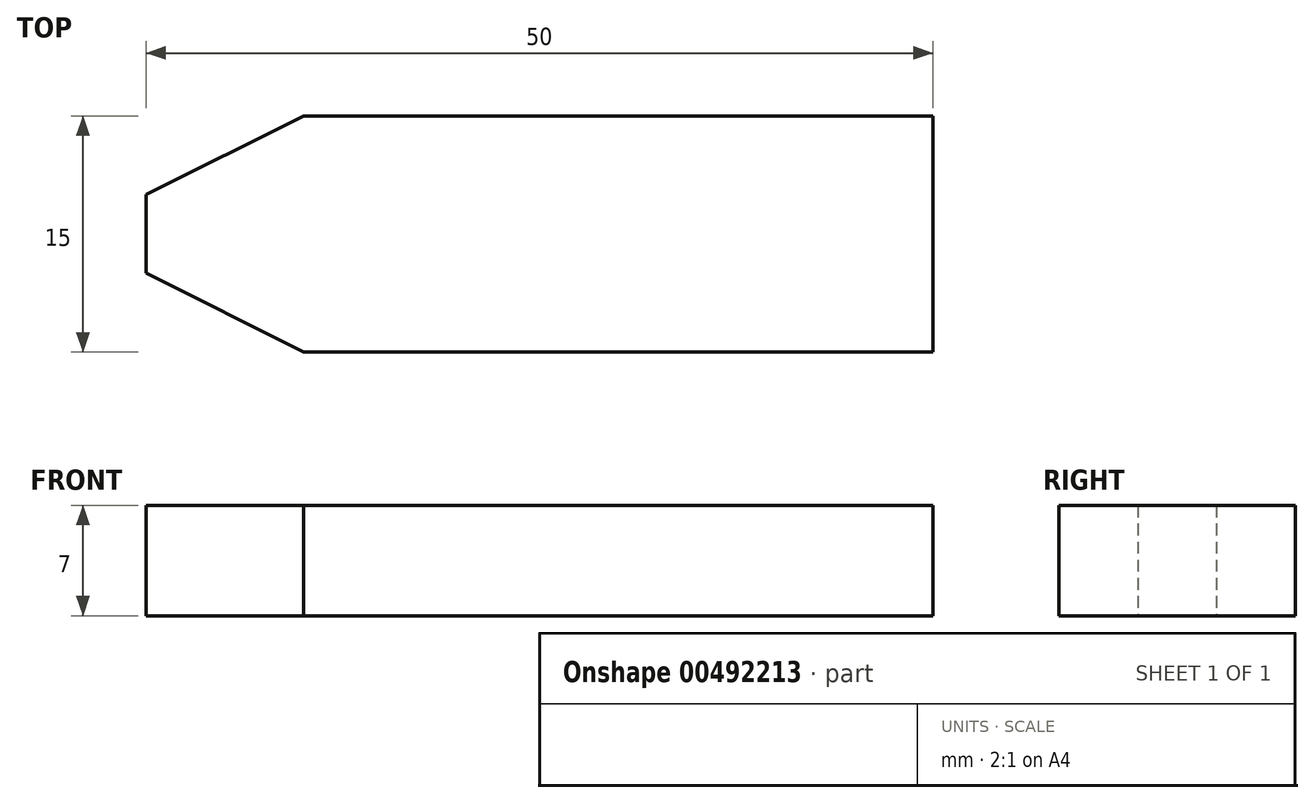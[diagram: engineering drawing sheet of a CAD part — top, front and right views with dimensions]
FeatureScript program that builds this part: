
annotation { "Feature Type Name" : "Feature", "Feature Type Description" : "" }
export const myFeature = defineFeature(function(context is Context, id is Id, definition is map)
    precondition{}
    {
        {
            var Q0;
            Q0=qCreatedBy(makeId("Top.planeOp"),FACE);
            var sketch = newSketch(context, id + "F0", { "sketchPlane" : qUnion([Q0])});
            skLineSegment(sketch, "E0.bottom", {"start": v(20, -7.5) * mm, "end": v(-20, -7.5) * mm});
            skLineSegment(sketch, "E0.top", {"start": v(20, 7.5) * mm, "end": v(-20, 7.5) * mm});
            skLineSegment(sketch, "E0.left", {"start": v(20, -7.5) * mm, "end": v(20, 7.5) * mm});
            skLineSegment(sketch, "E0.right", {"start": v(-20, -7.5) * mm, "end": v(-20, 7.5) * mm});
            skPoint(sketch, "E0.middle", {"position": v(0, 0) * mm});
            skLineSegment(sketch, "E1", {"start": v(-20, 7.5) * mm, "end": v(-20, 2.5) * mm});
            skLineSegment(sketch, "E2", {"start": v(-20, 2.5) * mm, "end": v(-20, -2.5) * mm});
            skLineSegment(sketch, "E3", {"start": v(-20, -2.5) * mm, "end": v(-20, -7.5) * mm});
            skLineSegment(sketch, "E4", {"start": v(-20, 2.5) * mm, "end": v(-30, 2.5) * mm});
            skLineSegment(sketch, "E5", {"start": v(-20, -2.5) * mm, "end": v(-30, -2.5) * mm});
            skLineSegment(sketch, "E6", {"start": v(-30, 2.5) * mm, "end": v(-20, 7.5) * mm});
            skLineSegment(sketch, "E7", {"start": v(-30, 2.5) * mm, "end": v(-30, -2.5) * mm});
            skLineSegment(sketch, "E8", {"start": v(-30, -2.5) * mm, "end": v(-20, -7.5) * mm});
            skSolve(sketch);
        }
        {
            var Q0;
            Q0 = qSketchRegion(id + "F0", true);
            extrude(context, id + "F1", {"entities" : qUnion([Q0]), "depth" : 7 * mm});
        }
    });
